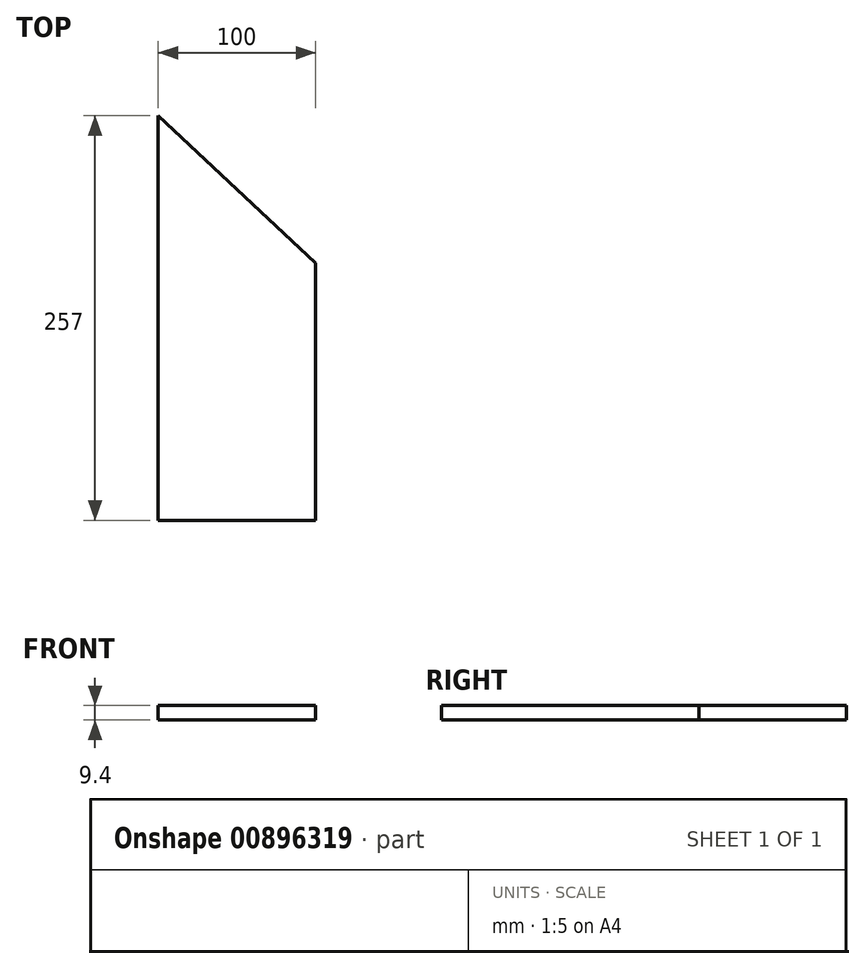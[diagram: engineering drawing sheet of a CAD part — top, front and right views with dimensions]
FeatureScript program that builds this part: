
annotation { "Feature Type Name" : "Feature", "Feature Type Description" : "" }
export const myFeature = defineFeature(function(context is Context, id is Id, definition is map)
    precondition{}
    {
        {
            var Q0;
            Q0=qCreatedBy(makeId("Top.planeOp"),FACE);
            var sketch = newSketch(context, id + "F0", { "sketchPlane" : qUnion([Q0])});
            skLineSegment(sketch, "E0.bottom", {"start": v(-50, 128.5) * mm, "end": v(50, 128.5) * mm});
            skLineSegment(sketch, "E0.top", {"start": v(-50, -128.5) * mm, "end": v(50, -128.5) * mm});
            skLineSegment(sketch, "E0.left", {"start": v(-50, 128.5) * mm, "end": v(-50, -128.5) * mm});
            skLineSegment(sketch, "E0.right", {"start": v(50, 128.5) * mm, "end": v(50, -128.5) * mm});
            skPoint(sketch, "E0.middle", {"position": v(0, 0) * mm});
            skLineSegment(sketch, "E1", {"start": v(-50, 128.5) * mm, "end": v(50, 35.04) * mm});
            skSolve(sketch);
        }
        {
            var Q0;
            {var subQ0=sQuery(id+"F0.wireOp",EDGE,"E0.top");Q0=makeQuery(id+"F0.imprint","IMPRINT",FACE,{"disambiguationData":[TD([[makeQuery(id+"F0.imprint","IMPRINT",EDGE,{"derivedFrom":subQ0}),1.0]])]});}
            extrude(context, id + "F1", {"entities" : qUnion([Q0]), "depth" : 9.4 * mm, "offsetDistance" : 25 * mm});
        }
    });
